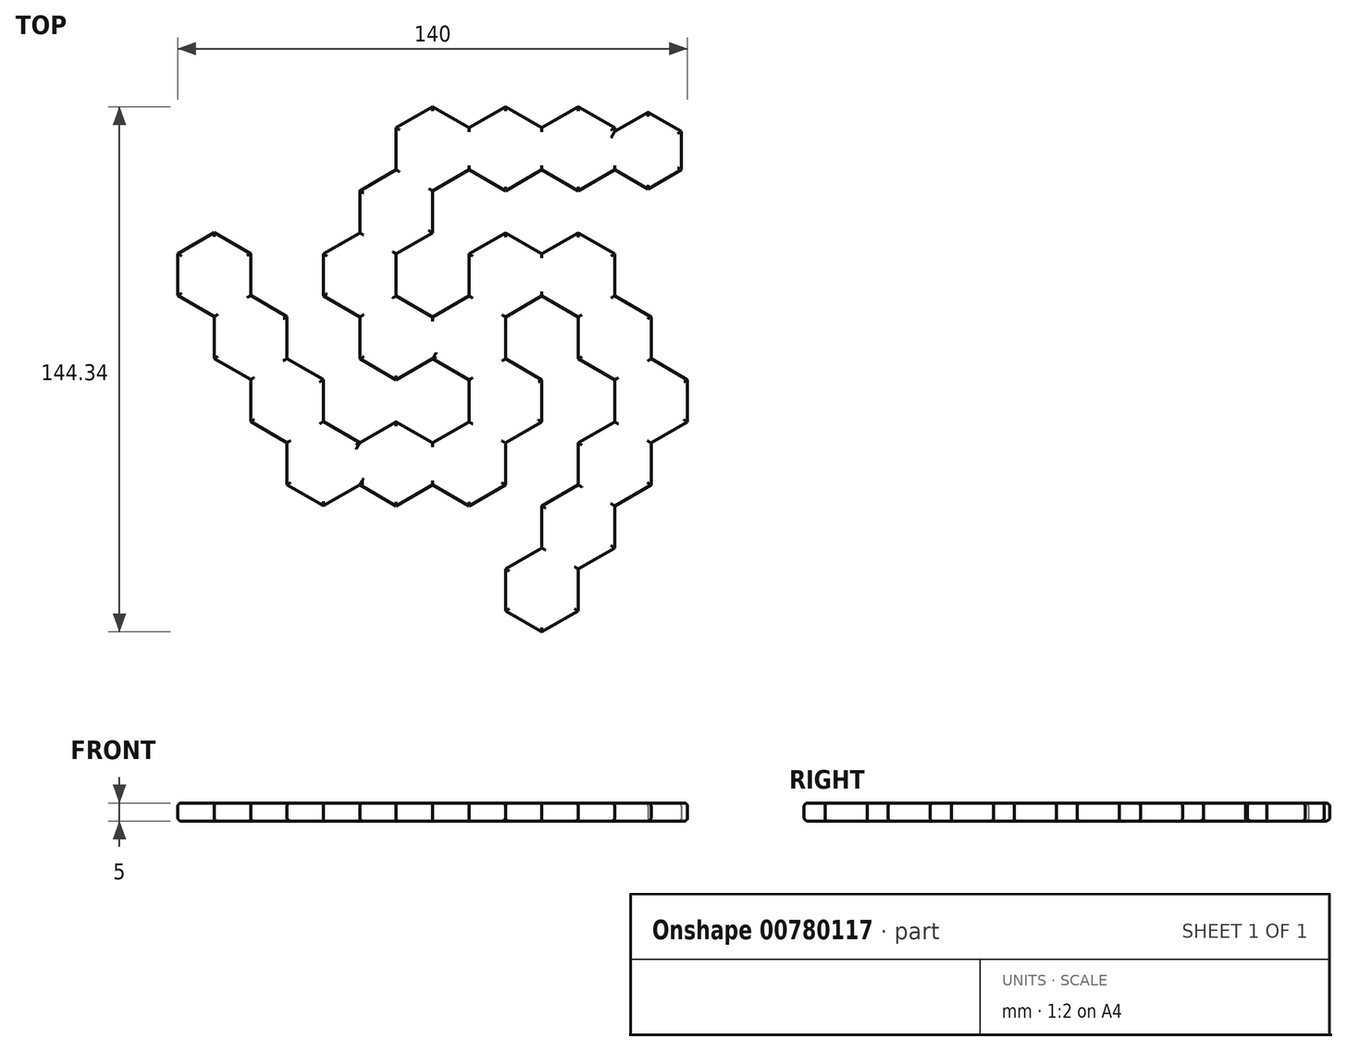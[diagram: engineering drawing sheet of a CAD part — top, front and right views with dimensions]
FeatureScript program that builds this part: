
annotation { "Feature Type Name" : "Feature", "Feature Type Description" : "" }
export const myFeature = defineFeature(function(context is Context, id is Id, definition is map)
    precondition{}
    {
        {
            var Q0;
            Q0=qCreatedBy(makeId("Top.planeOp"),FACE);
            var sketch = newSketch(context, id + "F0", { "sketchPlane" : qUnion([Q0])});
            skCircle(sketch, "E0.cCircle", {"center": v(0, 0) * mm, "radius": 10 * mm, "construction": true});
            skLineSegment(sketch, "E0.0", {"start": v(10, 5.77) * mm, "end": v(10, -5.77) * mm});
            skLineSegment(sketch, "E0.1", {"start": v(10, -5.77) * mm, "end": v(0, -11.55) * mm});
            skLineSegment(sketch, "E0.2", {"start": v(0, -11.55) * mm, "end": v(-10, -5.77) * mm});
            skLineSegment(sketch, "E0.3", {"start": v(-10, -5.77) * mm, "end": v(-10, 5.77) * mm});
            skLineSegment(sketch, "E0.4", {"start": v(-10, 5.77) * mm, "end": v(0, 11.55) * mm});
            skLineSegment(sketch, "E0.5", {"start": v(0, 11.55) * mm, "end": v(10, 5.77) * mm});
            skPoint(sketch, "E0.0.midPoint", {"position": v(10, 0) * mm});
            skCircle(sketch, "E1.cCircle", {"center": v(10, 17.32) * mm, "radius": 10 * mm, "construction": true});
            skLineSegment(sketch, "E1.0", {"start": v(20, 11.55) * mm, "end": v(10, 5.77) * mm});
            skLineSegment(sketch, "E1.1", {"start": v(10, 5.77) * mm, "end": v(0, 11.55) * mm});
            skLineSegment(sketch, "E1.2", {"start": v(0, 11.55) * mm, "end": v(0, 23.1) * mm});
            skLineSegment(sketch, "E1.3", {"start": v(0, 23.1) * mm, "end": v(10, 28.87) * mm});
            skLineSegment(sketch, "E1.4", {"start": v(10, 28.87) * mm, "end": v(20, 23.1) * mm});
            skLineSegment(sketch, "E1.5", {"start": v(20, 23.1) * mm, "end": v(20, 11.55) * mm});
            skPoint(sketch, "E1.0.midPoint", {"position": v(15, 8.66) * mm});
            skCircle(sketch, "E2.cCircle", {"center": v(10, -17.32) * mm, "radius": 10 * mm, "construction": true});
            skLineSegment(sketch, "E2.0", {"start": v(20, -11.55) * mm, "end": v(20, -23.1) * mm});
            skLineSegment(sketch, "E2.1", {"start": v(20, -23.1) * mm, "end": v(10, -28.87) * mm});
            skLineSegment(sketch, "E2.2", {"start": v(10, -28.87) * mm, "end": v(0, -23.1) * mm});
            skLineSegment(sketch, "E2.3", {"start": v(0, -23.1) * mm, "end": v(0, -11.55) * mm});
            skLineSegment(sketch, "E2.4", {"start": v(0, -11.55) * mm, "end": v(10, -5.77) * mm});
            skLineSegment(sketch, "E2.5", {"start": v(10, -5.77) * mm, "end": v(20, -11.55) * mm});
            skPoint(sketch, "E2.0.midPoint", {"position": v(20, -17.32) * mm});
            skCircle(sketch, "E3.cCircle", {"center": v(-20, 0) * mm, "radius": 10 * mm, "construction": true});
            skLineSegment(sketch, "E3.0", {"start": v(-10, 5.77) * mm, "end": v(-10, -5.77) * mm});
            skLineSegment(sketch, "E3.1", {"start": v(-10, -5.77) * mm, "end": v(-20, -11.55) * mm});
            skLineSegment(sketch, "E3.2", {"start": v(-20, -11.55) * mm, "end": v(-30, -5.77) * mm});
            skLineSegment(sketch, "E3.3", {"start": v(-30, -5.77) * mm, "end": v(-30, 5.77) * mm});
            skLineSegment(sketch, "E3.4", {"start": v(-30, 5.77) * mm, "end": v(-20, 11.55) * mm});
            skLineSegment(sketch, "E3.5", {"start": v(-20, 11.55) * mm, "end": v(-10, 5.77) * mm});
            skPoint(sketch, "E3.0.midPoint", {"position": v(-10, 0) * mm});
            skPoint(sketch, "E4.0.midPoint", {"position": v(7.03, -5.77) * mm});
            skPoint(sketch, "E5.0.midPoint", {"position": v(18.02, 8.38) * mm});
            skCircle(sketch, "E6.cCircle", {"center": v(30, 17.32) * mm, "radius": 10 * mm, "construction": true});
            skLineSegment(sketch, "E6.0", {"start": v(40, 23.1) * mm, "end": v(40, 11.55) * mm});
            skLineSegment(sketch, "E6.1", {"start": v(40, 11.55) * mm, "end": v(30, 5.77) * mm});
            skLineSegment(sketch, "E6.2", {"start": v(30, 5.77) * mm, "end": v(20, 11.55) * mm});
            skLineSegment(sketch, "E6.3", {"start": v(20, 11.55) * mm, "end": v(20, 23.1) * mm});
            skLineSegment(sketch, "E6.4", {"start": v(20, 23.1) * mm, "end": v(30, 28.87) * mm});
            skLineSegment(sketch, "E6.5", {"start": v(30, 28.87) * mm, "end": v(40, 23.1) * mm});
            skPoint(sketch, "E6.0.midPoint", {"position": v(40, 17.32) * mm});
            skCircle(sketch, "E7.cCircle", {"center": v(-30, 17.32) * mm, "radius": 10 * mm, "construction": true});
            skLineSegment(sketch, "E7.0", {"start": v(-20, 23.1) * mm, "end": v(-20, 11.55) * mm});
            skLineSegment(sketch, "E7.1", {"start": v(-20, 11.55) * mm, "end": v(-30, 5.77) * mm});
            skLineSegment(sketch, "E7.2", {"start": v(-30, 5.77) * mm, "end": v(-40, 11.55) * mm});
            skLineSegment(sketch, "E7.3", {"start": v(-40, 11.55) * mm, "end": v(-40, 23.1) * mm});
            skLineSegment(sketch, "E7.4", {"start": v(-40, 23.1) * mm, "end": v(-30, 28.87) * mm});
            skLineSegment(sketch, "E7.5", {"start": v(-30, 28.87) * mm, "end": v(-20, 23.1) * mm});
            skPoint(sketch, "E7.0.midPoint", {"position": v(-20, 17.32) * mm});
            skPoint(sketch, "E8.0.midPoint", {"position": v(-27.62, 1.8) * mm});
            skCircle(sketch, "E9.cCircle", {"center": v(0, -34.64) * mm, "radius": 10 * mm, "construction": true});
            skLineSegment(sketch, "E9.0", {"start": v(-10, -28.87) * mm, "end": v(0, -23.1) * mm});
            skLineSegment(sketch, "E9.1", {"start": v(0, -23.1) * mm, "end": v(10, -28.87) * mm});
            skLineSegment(sketch, "E9.2", {"start": v(10, -28.87) * mm, "end": v(10, -40.41) * mm});
            skLineSegment(sketch, "E9.3", {"start": v(10, -40.41) * mm, "end": v(0, -46.19) * mm});
            skLineSegment(sketch, "E9.4", {"start": v(0, -46.19) * mm, "end": v(-10, -40.41) * mm});
            skLineSegment(sketch, "E9.5", {"start": v(-10, -40.41) * mm, "end": v(-10, -28.87) * mm});
            skPoint(sketch, "E9.0.midPoint", {"position": v(-5, -25.98) * mm});
            skCircle(sketch, "E10.cCircle", {"center": v(-20, 34.64) * mm, "radius": 10 * mm, "construction": true});
            skLineSegment(sketch, "E10.0", {"start": v(-10, 28.87) * mm, "end": v(-20, 23.1) * mm});
            skLineSegment(sketch, "E10.1", {"start": v(-20, 23.1) * mm, "end": v(-30, 28.87) * mm});
            skLineSegment(sketch, "E10.2", {"start": v(-30, 28.87) * mm, "end": v(-30, 40.41) * mm});
            skLineSegment(sketch, "E10.3", {"start": v(-30, 40.41) * mm, "end": v(-20, 46.19) * mm});
            skLineSegment(sketch, "E10.4", {"start": v(-20, 46.19) * mm, "end": v(-10, 40.41) * mm});
            skLineSegment(sketch, "E10.5", {"start": v(-10, 40.41) * mm, "end": v(-10, 28.87) * mm});
            skPoint(sketch, "E10.0.midPoint", {"position": v(-15, 25.98) * mm});
            skCircle(sketch, "E11.cCircle", {"center": v(40, 0) * mm, "radius": 10 * mm, "construction": true});
            skLineSegment(sketch, "E11.0", {"start": v(40, 11.55) * mm, "end": v(50, 5.77) * mm});
            skLineSegment(sketch, "E11.1", {"start": v(50, 5.77) * mm, "end": v(50, -5.77) * mm});
            skLineSegment(sketch, "E11.2", {"start": v(50, -5.77) * mm, "end": v(40, -11.55) * mm});
            skLineSegment(sketch, "E11.3", {"start": v(40, -11.55) * mm, "end": v(30, -5.77) * mm});
            skLineSegment(sketch, "E11.4", {"start": v(30, -5.77) * mm, "end": v(30, 5.77) * mm});
            skLineSegment(sketch, "E11.5", {"start": v(30, 5.77) * mm, "end": v(40, 11.55) * mm});
            skPoint(sketch, "E11.0.midPoint", {"position": v(45, 8.66) * mm});
            skCircle(sketch, "E12.cCircle", {"center": v(-20, -34.64) * mm, "radius": 10 * mm, "construction": true});
            skLineSegment(sketch, "E12.0", {"start": v(-10, -28.87) * mm, "end": v(-10, -40.41) * mm});
            skLineSegment(sketch, "E12.1", {"start": v(-10, -40.41) * mm, "end": v(-20, -46.19) * mm});
            skLineSegment(sketch, "E12.2", {"start": v(-20, -46.19) * mm, "end": v(-30, -40.41) * mm});
            skLineSegment(sketch, "E12.3", {"start": v(-30, -40.41) * mm, "end": v(-30, -28.87) * mm});
            skLineSegment(sketch, "E12.4", {"start": v(-30, -28.87) * mm, "end": v(-20, -23.1) * mm});
            skLineSegment(sketch, "E12.5", {"start": v(-20, -23.1) * mm, "end": v(-10, -28.87) * mm});
            skPoint(sketch, "E12.0.midPoint", {"position": v(-10, -34.64) * mm});
            skCircle(sketch, "E13.cCircle", {"center": v(50, -17.32) * mm, "radius": 10 * mm, "construction": true});
            skLineSegment(sketch, "E13.0", {"start": v(50, -5.77) * mm, "end": v(60, -11.55) * mm});
            skLineSegment(sketch, "E13.1", {"start": v(60, -11.55) * mm, "end": v(60, -23.1) * mm});
            skLineSegment(sketch, "E13.2", {"start": v(60, -23.1) * mm, "end": v(50, -28.87) * mm});
            skLineSegment(sketch, "E13.3", {"start": v(50, -28.87) * mm, "end": v(40, -23.1) * mm});
            skLineSegment(sketch, "E13.4", {"start": v(40, -23.1) * mm, "end": v(40, -11.55) * mm});
            skLineSegment(sketch, "E13.5", {"start": v(40, -11.55) * mm, "end": v(50, -5.77) * mm});
            skPoint(sketch, "E13.0.midPoint", {"position": v(55, -8.66) * mm});
            skCircle(sketch, "E14.cCircle", {"center": v(-10, 51.96) * mm, "radius": 10 * mm, "construction": true});
            skLineSegment(sketch, "E14.0", {"start": v(0, 46.19) * mm, "end": v(-10, 40.41) * mm});
            skLineSegment(sketch, "E14.1", {"start": v(-10, 40.41) * mm, "end": v(-20, 46.19) * mm});
            skLineSegment(sketch, "E14.2", {"start": v(-20, 46.19) * mm, "end": v(-20, 57.73) * mm});
            skLineSegment(sketch, "E14.3", {"start": v(-20, 57.73) * mm, "end": v(-10, 63.5) * mm});
            skLineSegment(sketch, "E14.4", {"start": v(-10, 63.5) * mm, "end": v(0, 57.73) * mm});
            skLineSegment(sketch, "E14.5", {"start": v(0, 57.73) * mm, "end": v(0, 46.19) * mm});
            skPoint(sketch, "E14.0.midPoint", {"position": v(-5, 43.3) * mm});
            skCircle(sketch, "E15.cCircle", {"center": v(-40, -34.57) * mm, "radius": 10 * mm, "construction": true});
            skLineSegment(sketch, "E15.0", {"start": v(-30, -28.8) * mm, "end": v(-30, -40.34) * mm});
            skLineSegment(sketch, "E15.1", {"start": v(-30, -40.34) * mm, "end": v(-40, -46.11) * mm});
            skLineSegment(sketch, "E15.2", {"start": v(-40, -46.11) * mm, "end": v(-50, -40.34) * mm});
            skLineSegment(sketch, "E15.3", {"start": v(-50, -40.34) * mm, "end": v(-50, -28.8) * mm});
            skLineSegment(sketch, "E15.4", {"start": v(-50, -28.8) * mm, "end": v(-40, -23.02) * mm});
            skLineSegment(sketch, "E15.5", {"start": v(-40, -23.02) * mm, "end": v(-30, -28.8) * mm});
            skPoint(sketch, "E15.0.midPoint", {"position": v(-30, -34.57) * mm});
            skCircle(sketch, "E16.cCircle", {"center": v(-50, -17.24) * mm, "radius": 10 * mm, "construction": true});
            skLineSegment(sketch, "E16.0", {"start": v(-40, -23.02) * mm, "end": v(-50, -28.8) * mm});
            skLineSegment(sketch, "E16.1", {"start": v(-50, -28.8) * mm, "end": v(-60, -23.02) * mm});
            skLineSegment(sketch, "E16.2", {"start": v(-60, -23.02) * mm, "end": v(-60, -11.47) * mm});
            skLineSegment(sketch, "E16.3", {"start": v(-60, -11.47) * mm, "end": v(-50, -5.7) * mm});
            skLineSegment(sketch, "E16.4", {"start": v(-50, -5.7) * mm, "end": v(-40, -11.47) * mm});
            skLineSegment(sketch, "E16.5", {"start": v(-40, -11.47) * mm, "end": v(-40, -23.02) * mm});
            skPoint(sketch, "E16.0.midPoint", {"position": v(-45, -25.9) * mm});
            skCircle(sketch, "E17.cCircle", {"center": v(10, 51.96) * mm, "radius": 10 * mm, "construction": true});
            skPoint(sketch, "E17.cCircle.centerSnap0", {"position": v(-20, 51.96) * mm});
            skLineSegment(sketch, "E17.0", {"start": v(20, 46.19) * mm, "end": v(10, 40.41) * mm});
            skLineSegment(sketch, "E17.1", {"start": v(10, 40.41) * mm, "end": v(0, 46.19) * mm});
            skLineSegment(sketch, "E17.2", {"start": v(0, 46.19) * mm, "end": v(0, 57.73) * mm});
            skLineSegment(sketch, "E17.3", {"start": v(0, 57.73) * mm, "end": v(10, 63.5) * mm});
            skLineSegment(sketch, "E17.4", {"start": v(10, 63.5) * mm, "end": v(20, 57.73) * mm});
            skLineSegment(sketch, "E17.5", {"start": v(20, 57.73) * mm, "end": v(20, 46.19) * mm});
            skPoint(sketch, "E17.0.midPoint", {"position": v(15, 43.3) * mm});
            skCircle(sketch, "E18.cCircle", {"center": v(40, -34.64) * mm, "radius": 10 * mm, "construction": true});
            skLineSegment(sketch, "E18.0", {"start": v(50, -28.87) * mm, "end": v(50, -40.41) * mm});
            skLineSegment(sketch, "E18.1", {"start": v(50, -40.41) * mm, "end": v(40, -46.19) * mm});
            skLineSegment(sketch, "E18.2", {"start": v(40, -46.19) * mm, "end": v(30, -40.41) * mm});
            skLineSegment(sketch, "E18.3", {"start": v(30, -40.41) * mm, "end": v(30, -28.87) * mm});
            skLineSegment(sketch, "E18.4", {"start": v(30, -28.87) * mm, "end": v(40, -23.1) * mm});
            skLineSegment(sketch, "E18.5", {"start": v(40, -23.1) * mm, "end": v(50, -28.87) * mm});
            skPoint(sketch, "E18.0.midPoint", {"position": v(50, -34.64) * mm});
            skCircle(sketch, "E19.cCircle", {"center": v(30, 51.96) * mm, "radius": 10 * mm, "construction": true});
            skLineSegment(sketch, "E19.0", {"start": v(40, 57.73) * mm, "end": v(40, 46.19) * mm});
            skLineSegment(sketch, "E19.1", {"start": v(40, 46.19) * mm, "end": v(30, 40.41) * mm});
            skLineSegment(sketch, "E19.2", {"start": v(30, 40.41) * mm, "end": v(20, 46.19) * mm});
            skLineSegment(sketch, "E19.3", {"start": v(20, 46.19) * mm, "end": v(20, 57.73) * mm});
            skLineSegment(sketch, "E19.4", {"start": v(20, 57.73) * mm, "end": v(30, 63.5) * mm});
            skLineSegment(sketch, "E19.5", {"start": v(30, 63.5) * mm, "end": v(40, 57.73) * mm});
            skCircle(sketch, "E20.cCircle", {"center": v(30, -51.96) * mm, "radius": 10 * mm, "construction": true});
            skLineSegment(sketch, "E20.0", {"start": v(30, -63.5) * mm, "end": v(20, -57.74) * mm});
            skLineSegment(sketch, "E20.1", {"start": v(20, -57.74) * mm, "end": v(20, -46.19) * mm});
            skLineSegment(sketch, "E20.2", {"start": v(20, -46.19) * mm, "end": v(30, -40.41) * mm});
            skLineSegment(sketch, "E20.3", {"start": v(30, -40.41) * mm, "end": v(40, -46.19) * mm});
            skLineSegment(sketch, "E20.4", {"start": v(40, -46.19) * mm, "end": v(40, -57.74) * mm});
            skLineSegment(sketch, "E20.5", {"start": v(40, -57.74) * mm, "end": v(30, -63.5) * mm});
            skPoint(sketch, "E20.0.midPoint", {"position": v(25, -60.62) * mm});
            skCircle(sketch, "E21.cCircle", {"center": v(-60, 0.08) * mm, "radius": 10 * mm, "construction": true});
            skLineSegment(sketch, "E21.0", {"start": v(-50, -5.7) * mm, "end": v(-60, -11.47) * mm});
            skLineSegment(sketch, "E21.1", {"start": v(-60, -11.47) * mm, "end": v(-70, -5.7) * mm});
            skLineSegment(sketch, "E21.2", {"start": v(-70, -5.7) * mm, "end": v(-70, 5.85) * mm});
            skLineSegment(sketch, "E21.3", {"start": v(-70, 5.85) * mm, "end": v(-60, 11.62) * mm});
            skLineSegment(sketch, "E21.4", {"start": v(-60, 11.62) * mm, "end": v(-50, 5.85) * mm});
            skLineSegment(sketch, "E21.5", {"start": v(-50, 5.85) * mm, "end": v(-50, -5.7) * mm});
            skPoint(sketch, "E21.0.midPoint", {"position": v(-55, -8.58) * mm});
            skCircle(sketch, "E22.cCircle", {"center": v(-70, 17.4) * mm, "radius": 10 * mm, "construction": true});
            skLineSegment(sketch, "E22.0", {"start": v(-60, 11.62) * mm, "end": v(-70, 5.85) * mm});
            skLineSegment(sketch, "E22.1", {"start": v(-70, 5.85) * mm, "end": v(-80, 11.62) * mm});
            skLineSegment(sketch, "E22.2", {"start": v(-80, 11.62) * mm, "end": v(-80, 23.17) * mm});
            skLineSegment(sketch, "E22.3", {"start": v(-80, 23.17) * mm, "end": v(-70, 28.94) * mm});
            skLineSegment(sketch, "E22.4", {"start": v(-70, 28.94) * mm, "end": v(-60, 23.17) * mm});
            skLineSegment(sketch, "E22.5", {"start": v(-60, 23.17) * mm, "end": v(-60, 11.62) * mm});
            skPoint(sketch, "E22.0.midPoint", {"position": v(-65, 8.74) * mm});
            skCircle(sketch, "E23.cCircle", {"center": v(20, -69.28) * mm, "radius": 10 * mm, "construction": true});
            skLineSegment(sketch, "E23.0", {"start": v(20, -57.74) * mm, "end": v(30, -63.5) * mm});
            skLineSegment(sketch, "E23.1", {"start": v(30, -63.5) * mm, "end": v(30, -75.06) * mm});
            skLineSegment(sketch, "E23.2", {"start": v(30, -75.06) * mm, "end": v(20, -80.83) * mm});
            skLineSegment(sketch, "E23.3", {"start": v(20, -80.83) * mm, "end": v(10, -75.06) * mm});
            skLineSegment(sketch, "E23.4", {"start": v(10, -75.06) * mm, "end": v(10, -63.5) * mm});
            skLineSegment(sketch, "E23.5", {"start": v(10, -63.5) * mm, "end": v(20, -57.74) * mm});
            skCircle(sketch, "E24.cCircle", {"center": v(49.15, 51.47) * mm, "radius": 9.15 * mm, "construction": true});
            skLineSegment(sketch, "E24.0", {"start": v(58.3, 46.19) * mm, "end": v(49.15, 40.9) * mm});
            skLineSegment(sketch, "E24.1", {"start": v(49.15, 40.9) * mm, "end": v(40, 46.19) * mm});
            skLineSegment(sketch, "E24.2", {"start": v(40, 46.19) * mm, "end": v(40, 56.75) * mm});
            skLineSegment(sketch, "E24.3", {"start": v(40, 56.75) * mm, "end": v(49.15, 62.03) * mm});
            skLineSegment(sketch, "E24.4", {"start": v(49.15, 62.03) * mm, "end": v(58.3, 56.75) * mm});
            skLineSegment(sketch, "E24.5", {"start": v(58.3, 56.75) * mm, "end": v(58.3, 46.19) * mm});
            skPoint(sketch, "E24.0.midPoint", {"position": v(53.72, 43.55) * mm});
            skSolve(sketch);
        }
        {
            var Q0;
            Q0 = qSketchRegion(id + "F0", true);
            extrude(context, id + "F1", {"entities" : qUnion([Q0]), "depth" : 5 * mm, "offsetDistance" : 25 * mm});
        }
        {
            var Q0;
            Q0=makeQuery(id+"F1.opExtrude","CAP_FACE",FACE,{"disambiguationData":[OSD([sQuery(id+"F0.wireOp",EDGE,"E0.0"),sQuery(id+"F0.wireOp",EDGE,"E0.2"),sQuery(id+"F0.wireOp",EDGE,"E0.3"),sQuery(id+"F0.wireOp",EDGE,"E0.4"),sQuery(id+"F0.wireOp",EDGE,"E1.0"),sQuery(id+"F0.wireOp",EDGE,"E1.2"),sQuery(id+"F0.wireOp",EDGE,"E1.3"),sQuery(id+"F0.wireOp",EDGE,"E1.4"),sQuery(id+"F0.wireOp",EDGE,"E2.0"),sQuery(id+"F0.wireOp",EDGE,"E2.1"),sQuery(id+"F0.wireOp",EDGE,"E2.3"),sQuery(id+"F0.wireOp",EDGE,"E2.5"),sQuery(id+"F0.wireOp",EDGE,"E3.1"),sQuery(id+"F0.wireOp",EDGE,"E3.2"),sQuery(id+"F0.wireOp",EDGE,"E3.3"),sQuery(id+"F0.wireOp",EDGE,"E3.5"),sQuery(id+"F0.wireOp",EDGE,"E6.0"),sQuery(id+"F0.wireOp",EDGE,"E6.2"),sQuery(id+"F0.wireOp",EDGE,"E6.4"),sQuery(id+"F0.wireOp",EDGE,"E6.5"),sQuery(id+"F0.wireOp",EDGE,"E7.0"),sQuery(id+"F0.wireOp",EDGE,"E7.2"),sQuery(id+"F0.wireOp",EDGE,"E7.3"),sQuery(id+"F0.wireOp",EDGE,"E7.4"),sQuery(id+"F0.wireOp",EDGE,"E9.0"),sQuery(id+"F0.wireOp",EDGE,"E9.2"),sQuery(id+"F0.wireOp",EDGE,"E9.3"),sQuery(id+"F0.wireOp",EDGE,"E9.4"),sQuery(id+"F0.wireOp",EDGE,"E10.0"),sQuery(id+"F0.wireOp",EDGE,"E10.2"),sQuery(id+"F0.wireOp",EDGE,"E10.3"),sQuery(id+"F0.wireOp",EDGE,"E10.5"),sQuery(id+"F0.wireOp",EDGE,"E11.0"),sQuery(id+"F0.wireOp",EDGE,"E11.1"),sQuery(id+"F0.wireOp",EDGE,"E11.3"),sQuery(id+"F0.wireOp",EDGE,"E11.4"),sQuery(id+"F0.wireOp",EDGE,"E12.1"),sQuery(id+"F0.wireOp",EDGE,"E12.2"),sQuery(id+"F0.wireOp",EDGE,"E12.3"),sQuery(id+"F0.wireOp",EDGE,"E12.4"),sQuery(id+"F0.wireOp",EDGE,"E12.5"),sQuery(id+"F0.wireOp",EDGE,"E13.0"),sQuery(id+"F0.wireOp",EDGE,"E13.1"),sQuery(id+"F0.wireOp",EDGE,"E13.2"),sQuery(id+"F0.wireOp",EDGE,"E13.4"),sQuery(id+"F0.wireOp",EDGE,"E14.0"),sQuery(id+"F0.wireOp",EDGE,"E14.2"),sQuery(id+"F0.wireOp",EDGE,"E14.3"),sQuery(id+"F0.wireOp",EDGE,"E14.4"),sQuery(id+"F0.wireOp",EDGE,"E15.0"),sQuery(id+"F0.wireOp",EDGE,"E15.1"),sQuery(id+"F0.wireOp",EDGE,"E15.2"),sQuery(id+"F0.wireOp",EDGE,"E15.3"),sQuery(id+"F0.wireOp",EDGE,"E15.5"),sQuery(id+"F0.wireOp",EDGE,"E16.1"),sQuery(id+"F0.wireOp",EDGE,"E16.2"),sQuery(id+"F0.wireOp",EDGE,"E16.4"),sQuery(id+"F0.wireOp",EDGE,"E16.5"),sQuery(id+"F0.wireOp",EDGE,"E17.0"),sQuery(id+"F0.wireOp",EDGE,"E17.1"),sQuery(id+"F0.wireOp",EDGE,"E17.3"),sQuery(id+"F0.wireOp",EDGE,"E17.4"),sQuery(id+"F0.wireOp",EDGE,"E18.0"),sQuery(id+"F0.wireOp",EDGE,"E18.1"),sQuery(id+"F0.wireOp",EDGE,"E18.3"),sQuery(id+"F0.wireOp",EDGE,"E18.4"),sQuery(id+"F0.wireOp",EDGE,"E19.1"),sQuery(id+"F0.wireOp",EDGE,"E19.2"),sQuery(id+"F0.wireOp",EDGE,"E19.4"),sQuery(id+"F0.wireOp",EDGE,"E19.5"),sQuery(id+"F0.wireOp",EDGE,"E20.1"),sQuery(id+"F0.wireOp",EDGE,"E20.2"),sQuery(id+"F0.wireOp",EDGE,"E20.4"),sQuery(id+"F0.wireOp",EDGE,"E20.5"),sQuery(id+"F0.wireOp",EDGE,"E21.1"),sQuery(id+"F0.wireOp",EDGE,"E21.2"),sQuery(id+"F0.wireOp",EDGE,"E21.4"),sQuery(id+"F0.wireOp",EDGE,"E21.5"),sQuery(id+"F0.wireOp",EDGE,"E22.1"),sQuery(id+"F0.wireOp",EDGE,"E22.2"),sQuery(id+"F0.wireOp",EDGE,"E22.3"),sQuery(id+"F0.wireOp",EDGE,"E22.4"),sQuery(id+"F0.wireOp",EDGE,"E22.5"),sQuery(id+"F0.wireOp",EDGE,"E23.1"),sQuery(id+"F0.wireOp",EDGE,"E23.2"),sQuery(id+"F0.wireOp",EDGE,"E23.3"),sQuery(id+"F0.wireOp",EDGE,"E23.4"),sQuery(id+"F0.wireOp",EDGE,"E23.5"),sQuery(id+"F0.wireOp",EDGE,"E24.0"),sQuery(id+"F0.wireOp",EDGE,"E24.1"),sQuery(id+"F0.wireOp",EDGE,"E24.3"),sQuery(id+"F0.wireOp",EDGE,"E24.4"),sQuery(id+"F0.wireOp",EDGE,"E24.5")])],"isStart":false});
            var Q1;
            Q1=makeQuery(id+"F1.opExtrude","CAP_FACE",FACE,{"disambiguationData":[OSD([sQuery(id+"F0.wireOp",EDGE,"E0.0"),sQuery(id+"F0.wireOp",EDGE,"E0.2"),sQuery(id+"F0.wireOp",EDGE,"E0.3"),sQuery(id+"F0.wireOp",EDGE,"E0.4"),sQuery(id+"F0.wireOp",EDGE,"E1.0"),sQuery(id+"F0.wireOp",EDGE,"E1.2"),sQuery(id+"F0.wireOp",EDGE,"E1.3"),sQuery(id+"F0.wireOp",EDGE,"E1.4"),sQuery(id+"F0.wireOp",EDGE,"E2.0"),sQuery(id+"F0.wireOp",EDGE,"E2.1"),sQuery(id+"F0.wireOp",EDGE,"E2.3"),sQuery(id+"F0.wireOp",EDGE,"E2.5"),sQuery(id+"F0.wireOp",EDGE,"E3.1"),sQuery(id+"F0.wireOp",EDGE,"E3.2"),sQuery(id+"F0.wireOp",EDGE,"E3.3"),sQuery(id+"F0.wireOp",EDGE,"E3.5"),sQuery(id+"F0.wireOp",EDGE,"E6.0"),sQuery(id+"F0.wireOp",EDGE,"E6.2"),sQuery(id+"F0.wireOp",EDGE,"E6.4"),sQuery(id+"F0.wireOp",EDGE,"E6.5"),sQuery(id+"F0.wireOp",EDGE,"E7.0"),sQuery(id+"F0.wireOp",EDGE,"E7.2"),sQuery(id+"F0.wireOp",EDGE,"E7.3"),sQuery(id+"F0.wireOp",EDGE,"E7.4"),sQuery(id+"F0.wireOp",EDGE,"E9.0"),sQuery(id+"F0.wireOp",EDGE,"E9.2"),sQuery(id+"F0.wireOp",EDGE,"E9.3"),sQuery(id+"F0.wireOp",EDGE,"E9.4"),sQuery(id+"F0.wireOp",EDGE,"E10.0"),sQuery(id+"F0.wireOp",EDGE,"E10.2"),sQuery(id+"F0.wireOp",EDGE,"E10.3"),sQuery(id+"F0.wireOp",EDGE,"E10.5"),sQuery(id+"F0.wireOp",EDGE,"E11.0"),sQuery(id+"F0.wireOp",EDGE,"E11.1"),sQuery(id+"F0.wireOp",EDGE,"E11.3"),sQuery(id+"F0.wireOp",EDGE,"E11.4"),sQuery(id+"F0.wireOp",EDGE,"E12.1"),sQuery(id+"F0.wireOp",EDGE,"E12.2"),sQuery(id+"F0.wireOp",EDGE,"E12.3"),sQuery(id+"F0.wireOp",EDGE,"E12.4"),sQuery(id+"F0.wireOp",EDGE,"E12.5"),sQuery(id+"F0.wireOp",EDGE,"E13.0"),sQuery(id+"F0.wireOp",EDGE,"E13.1"),sQuery(id+"F0.wireOp",EDGE,"E13.2"),sQuery(id+"F0.wireOp",EDGE,"E13.4"),sQuery(id+"F0.wireOp",EDGE,"E14.0"),sQuery(id+"F0.wireOp",EDGE,"E14.2"),sQuery(id+"F0.wireOp",EDGE,"E14.3"),sQuery(id+"F0.wireOp",EDGE,"E14.4"),sQuery(id+"F0.wireOp",EDGE,"E15.0"),sQuery(id+"F0.wireOp",EDGE,"E15.1"),sQuery(id+"F0.wireOp",EDGE,"E15.2"),sQuery(id+"F0.wireOp",EDGE,"E15.3"),sQuery(id+"F0.wireOp",EDGE,"E15.5"),sQuery(id+"F0.wireOp",EDGE,"E16.1"),sQuery(id+"F0.wireOp",EDGE,"E16.2"),sQuery(id+"F0.wireOp",EDGE,"E16.4"),sQuery(id+"F0.wireOp",EDGE,"E16.5"),sQuery(id+"F0.wireOp",EDGE,"E17.0"),sQuery(id+"F0.wireOp",EDGE,"E17.1"),sQuery(id+"F0.wireOp",EDGE,"E17.3"),sQuery(id+"F0.wireOp",EDGE,"E17.4"),sQuery(id+"F0.wireOp",EDGE,"E18.0"),sQuery(id+"F0.wireOp",EDGE,"E18.1"),sQuery(id+"F0.wireOp",EDGE,"E18.3"),sQuery(id+"F0.wireOp",EDGE,"E18.4"),sQuery(id+"F0.wireOp",EDGE,"E19.1"),sQuery(id+"F0.wireOp",EDGE,"E19.2"),sQuery(id+"F0.wireOp",EDGE,"E19.4"),sQuery(id+"F0.wireOp",EDGE,"E19.5"),sQuery(id+"F0.wireOp",EDGE,"E20.1"),sQuery(id+"F0.wireOp",EDGE,"E20.2"),sQuery(id+"F0.wireOp",EDGE,"E20.4"),sQuery(id+"F0.wireOp",EDGE,"E20.5"),sQuery(id+"F0.wireOp",EDGE,"E21.1"),sQuery(id+"F0.wireOp",EDGE,"E21.2"),sQuery(id+"F0.wireOp",EDGE,"E21.4"),sQuery(id+"F0.wireOp",EDGE,"E21.5"),sQuery(id+"F0.wireOp",EDGE,"E22.1"),sQuery(id+"F0.wireOp",EDGE,"E22.2"),sQuery(id+"F0.wireOp",EDGE,"E22.3"),sQuery(id+"F0.wireOp",EDGE,"E22.4"),sQuery(id+"F0.wireOp",EDGE,"E22.5"),sQuery(id+"F0.wireOp",EDGE,"E23.1"),sQuery(id+"F0.wireOp",EDGE,"E23.2"),sQuery(id+"F0.wireOp",EDGE,"E23.3"),sQuery(id+"F0.wireOp",EDGE,"E23.4"),sQuery(id+"F0.wireOp",EDGE,"E23.5"),sQuery(id+"F0.wireOp",EDGE,"E24.0"),sQuery(id+"F0.wireOp",EDGE,"E24.1"),sQuery(id+"F0.wireOp",EDGE,"E24.3"),sQuery(id+"F0.wireOp",EDGE,"E24.4"),sQuery(id+"F0.wireOp",EDGE,"E24.5")])],"isStart":true});
            fillet(context, id + "F2", {"entities" : qUnion([Q0, Q1]), "radius" : 1 * mm, "tangentPropagation" : true, "allowEdgeOverflow" : false});
        }
    });
